# Revit family: Andreu World_Alya_BU1520
name_source: partatom
category: Mobiliario
revit_build: Autodesk Revit 2014 (Build: 20130722_2115(x64)
units: mm (PartAtom-declared; Revit-internal decimal feet)

## types (1)
- Andreu World_Alya_BU1520
    Arm Height = 480 mm
    Base Material = Andreu World Polished Aluminum
    Depth = 800 mm  [stored 2.62467 ft]
    Descripción = High back lounge chair with upholstered seat and backrest, and aluminum central swivel base with self-return system
    Fabricante = Andreu World
    Glides = Andreu World Plastic Glides
    Height = 1100 mm
    Modelo = Alya
    Reference = BU-1520
    Seat Height = 430 mm
    Seat Material = Andreu World Fabric
    URL = http://www.andreuworld.com
    Width = 750 mm  [stored 2.46063 ft]

note: [stored X ft] marks values corroborated as IEEE doubles in the binary element streams (Revit-internal decimal feet)

## geometry (parser evidence)
native form markers: Blend x2, Sweep x3
no freeform markers — native parametric forms only
